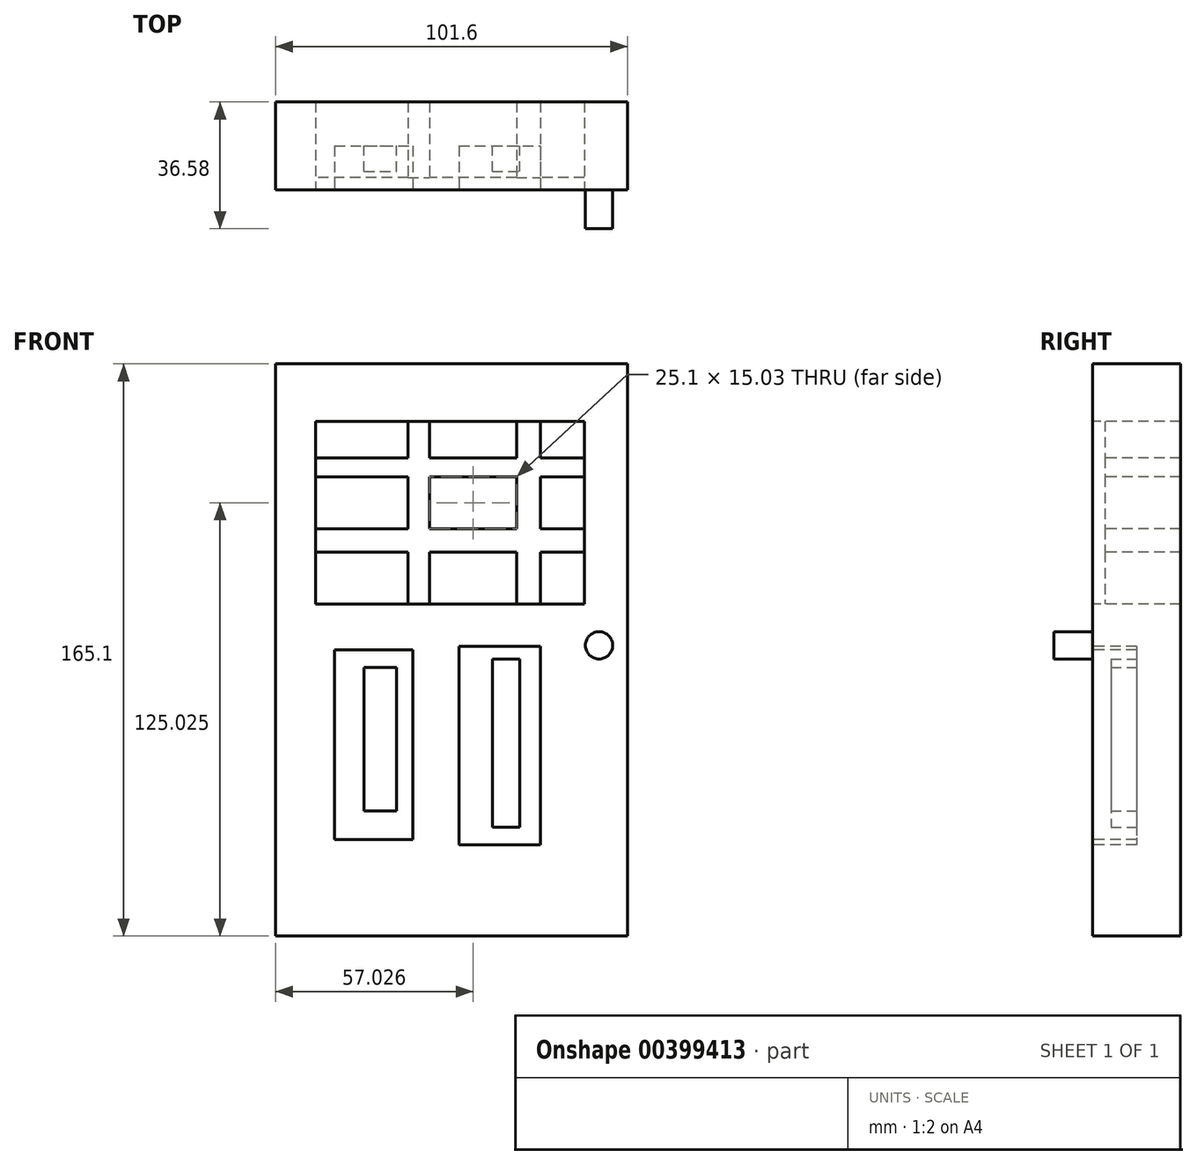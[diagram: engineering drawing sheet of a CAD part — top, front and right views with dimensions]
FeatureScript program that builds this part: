
annotation { "Feature Type Name" : "Feature", "Feature Type Description" : "" }
export const myFeature = defineFeature(function(context is Context, id is Id, definition is map)
    precondition{}
    {
        {
            var Q0;
            Q0=qCreatedBy(makeId("Front.planeOp"),FACE);
            var sketch = newSketch(context, id + "F0", { "sketchPlane" : qUnion([Q0])});
            skLineSegment(sketch, "E0.bottom", {"start": v(-76.52, 69.29) * mm, "end": v(25.08, 69.29) * mm});
            skLineSegment(sketch, "E0.top", {"start": v(-76.52, -95.81) * mm, "end": v(25.08, -95.81) * mm});
            skLineSegment(sketch, "E0.left", {"start": v(-76.52, 69.29) * mm, "end": v(-76.52, -95.81) * mm});
            skLineSegment(sketch, "E0.right", {"start": v(25.08, 69.29) * mm, "end": v(25.08, -95.81) * mm});
            skSolve(sketch);
        }
        {
            var Q0;
            Q0 = qSketchRegion(id + "F0", true);
            extrude(context, id + "F1", {"entities" : qUnion([Q0]), "depth" : 25.4 * mm});
        }
        {
            var Q0;
            Q0=makeQuery(id+"F1.opExtrude","CAP_FACE",FACE,{"disambiguationData":[OSD([sQuery(id+"F0.wireOp",EDGE,"E0.bottom"),sQuery(id+"F0.wireOp",EDGE,"E0.top"),sQuery(id+"F0.wireOp",EDGE,"E0.left"),sQuery(id+"F0.wireOp",EDGE,"E0.right")])],"isStart":false});
            var sketch = newSketch(context, id + "F2", { "sketchPlane" : qUnion([Q0])});
            skLineSegment(sketch, "E1.bottom", {"start": v(-64.93, 52.75) * mm, "end": v(12.65, 52.75) * mm});
            skLineSegment(sketch, "E1.top", {"start": v(-64.93, 0) * mm, "end": v(12.65, 0) * mm});
            skLineSegment(sketch, "E1.left", {"start": v(-64.93, 52.75) * mm, "end": v(-64.93, 0) * mm});
            skLineSegment(sketch, "E1.right", {"start": v(12.65, 52.75) * mm, "end": v(12.65, 0) * mm});
            skSolve(sketch);
        }
        {
            var Q0;
            Q0 = qSketchRegion(id + "F2", true);
            extrude(context, id + "F3", {"entities" : qUnion([Q0]), "operationType" : NewBodyOperationType.REMOVE, "oppositeDirection" : true, "depth" : 61.98 * mm});
        }
        {
            var Q0;
            Q0=makeQuery(id+"F1.opExtrude","CAP_FACE",FACE,{"disambiguationData":[OSD([sQuery(id+"F0.wireOp",EDGE,"E0.bottom"),sQuery(id+"F0.wireOp",EDGE,"E0.top"),sQuery(id+"F0.wireOp",EDGE,"E0.left"),sQuery(id+"F0.wireOp",EDGE,"E0.right")])],"isStart":true});
            var sketch = newSketch(context, id + "F4", { "sketchPlane" : qUnion([Q0])});
            skLineSegment(sketch, "E2.bottom", {"start": v(-15.6, 42.2) * mm, "end": v(68.34, 42.2) * mm});
            skLineSegment(sketch, "E2.top", {"start": v(-15.6, 36.73) * mm, "end": v(68.34, 36.73) * mm});
            skLineSegment(sketch, "E2.left", {"start": v(-15.6, 42.2) * mm, "end": v(-15.6, 36.73) * mm});
            skLineSegment(sketch, "E2.right", {"start": v(68.34, 42.2) * mm, "end": v(68.34, 36.73) * mm});
            skLineSegment(sketch, "E3.bottom", {"start": v(-15.6, 21.7) * mm, "end": v(68.34, 21.7) * mm});
            skLineSegment(sketch, "E3.top", {"start": v(-15.6, 15.03) * mm, "end": v(68.34, 15.03) * mm});
            skLineSegment(sketch, "E3.left", {"start": v(-15.6, 21.7) * mm, "end": v(-15.6, 15.03) * mm});
            skLineSegment(sketch, "E3.right", {"start": v(68.34, 21.7) * mm, "end": v(68.34, 15.03) * mm});
            skLineSegment(sketch, "E4.bottom", {"start": v(0, 57.04) * mm, "end": v(6.94, 57.04) * mm});
            skLineSegment(sketch, "E4.top", {"start": v(0, -6.58) * mm, "end": v(6.94, -6.58) * mm});
            skLineSegment(sketch, "E4.left", {"start": v(0, 57.04) * mm, "end": v(0, -6.58) * mm});
            skLineSegment(sketch, "E4.right", {"start": v(6.94, 57.04) * mm, "end": v(6.94, -6.58) * mm});
            skLineSegment(sketch, "E5.bottom", {"start": v(32.04, 56.6) * mm, "end": v(38.25, 56.6) * mm});
            skLineSegment(sketch, "E5.top", {"start": v(32.04, -5.73) * mm, "end": v(38.25, -5.73) * mm});
            skLineSegment(sketch, "E5.left", {"start": v(32.04, 56.6) * mm, "end": v(32.04, -5.73) * mm});
            skLineSegment(sketch, "E5.right", {"start": v(38.25, 56.6) * mm, "end": v(38.25, -5.73) * mm});
            skSolve(sketch);
        }
        {
            var Q0;
            Q0 = qSketchRegion(id + "F4", true);
            extrude(context, id + "F5", {"entities" : qUnion([Q0]), "operationType" : NewBodyOperationType.ADD, "oppositeDirection" : true, "depth" : 21.84 * mm});
        }
        {
            var Q0;
            Q0=makeQuery(id+"F1.opExtrude","CAP_FACE",FACE,{"disambiguationData":[OSD([sQuery(id+"F0.wireOp",EDGE,"E0.bottom"),sQuery(id+"F0.wireOp",EDGE,"E0.top"),sQuery(id+"F0.wireOp",EDGE,"E0.left"),sQuery(id+"F0.wireOp",EDGE,"E0.right")])],"isStart":false});
            var sketch = newSketch(context, id + "F6", { "sketchPlane" : qUnion([Q0])});
            skPoint(sketch, "E6.firstSnap0", {"position": v(-76.52, -13.26) * mm});
            skLineSegment(sketch, "E6.bottom", {"start": v(-59.43, -13.26) * mm, "end": v(-36.91, -13.26) * mm});
            skLineSegment(sketch, "E6.top", {"start": v(-59.43, -67.94) * mm, "end": v(-36.91, -67.94) * mm});
            skLineSegment(sketch, "E6.left", {"start": v(-59.43, -13.26) * mm, "end": v(-59.43, -67.94) * mm});
            skLineSegment(sketch, "E6.right", {"start": v(-36.91, -13.26) * mm, "end": v(-36.91, -67.94) * mm});
            skLineSegment(sketch, "E7.bottom", {"start": v(-23.52, -12.26) * mm, "end": v(0, -12.26) * mm});
            skLineSegment(sketch, "E7.top", {"start": v(-23.52, -69.43) * mm, "end": v(0, -69.43) * mm});
            skLineSegment(sketch, "E7.left", {"start": v(-23.52, -12.26) * mm, "end": v(-23.52, -69.43) * mm});
            skLineSegment(sketch, "E7.right", {"start": v(0, -12.26) * mm, "end": v(0, -69.43) * mm});
            skSolve(sketch);
        }
        {
            var Q0;
            Q0 = qSketchRegion(id + "F6", true);
            extrude(context, id + "F7", {"entities" : qUnion([Q0]), "operationType" : NewBodyOperationType.REMOVE, "oppositeDirection" : true, "depth" : 12.7 * mm});
        }
        {
            var Q0;
            Q0=makeQuery(id+"F7.boolean.opBoolean","COPY",FACE,{"derivedFrom":makeQuery(id+"F7.opExtrude","CAP_FACE",FACE,{"disambiguationData":[OSD([sQuery(id+"F6.wireOp",EDGE,"E6.bottom"),sQuery(id+"F6.wireOp",EDGE,"E6.top"),sQuery(id+"F6.wireOp",EDGE,"E6.left"),sQuery(id+"F6.wireOp",EDGE,"E6.right")])],"isStart":false})});
            var sketch = newSketch(context, id + "F8", { "sketchPlane" : qUnion([Q0])});
            skLineSegment(sketch, "E8.bottom", {"start": v(-50.96, -18.33) * mm, "end": v(-41.64, -18.33) * mm});
            skLineSegment(sketch, "E8.top", {"start": v(-50.96, -59.68) * mm, "end": v(-41.64, -59.68) * mm});
            skLineSegment(sketch, "E8.left", {"start": v(-50.96, -18.33) * mm, "end": v(-50.96, -59.68) * mm});
            skLineSegment(sketch, "E8.right", {"start": v(-41.64, -18.33) * mm, "end": v(-41.64, -59.68) * mm});
            skLineSegment(sketch, "E9.bottom", {"start": v(-13.96, -15.94) * mm, "end": v(-6, -15.94) * mm});
            skLineSegment(sketch, "E9.top", {"start": v(-13.96, -64.45) * mm, "end": v(-6, -64.45) * mm});
            skLineSegment(sketch, "E9.left", {"start": v(-13.96, -15.94) * mm, "end": v(-13.96, -64.45) * mm});
            skLineSegment(sketch, "E9.right", {"start": v(-6, -15.94) * mm, "end": v(-6, -64.45) * mm});
            skSolve(sketch);
        }
        {
            var Q0;
            Q0 = qSketchRegion(id + "F8", true);
            extrude(context, id + "F9", {"entities" : qUnion([Q0]), "operationType" : NewBodyOperationType.ADD, "depth" : 7.37 * mm});
        }
        {
            var Q0;
            Q0=makeQuery(id+"F1.opExtrude","CAP_FACE",FACE,{"disambiguationData":[OSD([sQuery(id+"F0.wireOp",EDGE,"E0.bottom"),sQuery(id+"F0.wireOp",EDGE,"E0.top"),sQuery(id+"F0.wireOp",EDGE,"E0.left"),sQuery(id+"F0.wireOp",EDGE,"E0.right")])],"isStart":false});
            var sketch = newSketch(context, id + "F10", { "sketchPlane" : qUnion([Q0])});
            skCircle(sketch, "E10", {"center": v(16.88, -11.9) * mm, "radius": 3.93 * mm});
            skSolve(sketch);
        }
        {
            var Q0;
            Q0 = qSketchRegion(id + "F10", true);
            extrude(context, id + "F11", {"entities" : qUnion([Q0]), "operationType" : NewBodyOperationType.ADD, "depth" : 11.18 * mm});
        }
    });
